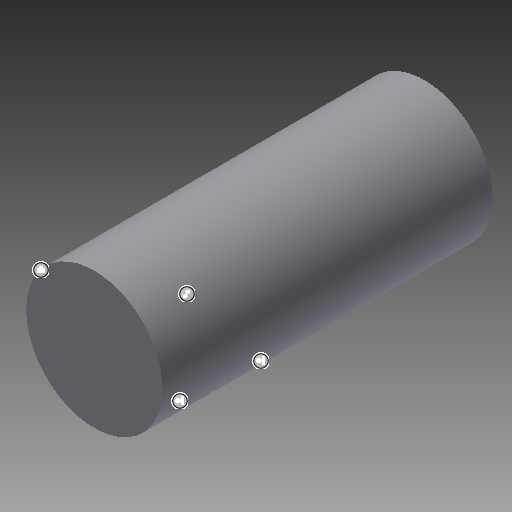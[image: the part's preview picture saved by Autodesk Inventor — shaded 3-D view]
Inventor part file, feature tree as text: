
AUTODESK INVENTOR PART (.ipt)
format: ipt  version: 2017 (Build 210142000, 142)  size: 104,448 bytes
history: native  units: mm
features: extrude x1, sketch x1
ambient origin geometry x8: Origin, YZ Plane, XZ Plane, XY Plane, X Axis, Y Axis, Z Axis, Center Point
bodies: Solid1 (feature_tree)
feature tree (2):
  extrude  "Extrusion1"  TaperAngle=0.0deg  [1 undecoded]
  sketch  "Sketch1"  dims[d2=0.0mm d3=0.0mm d4=0.0mm d9=0.0mm d10=0.0mm]
note: 1 required parameter value undecoded (feature->parameter linkage not recoverable at this tier; creation-order binding heuristic only, values carry confidence <= 0.55)
